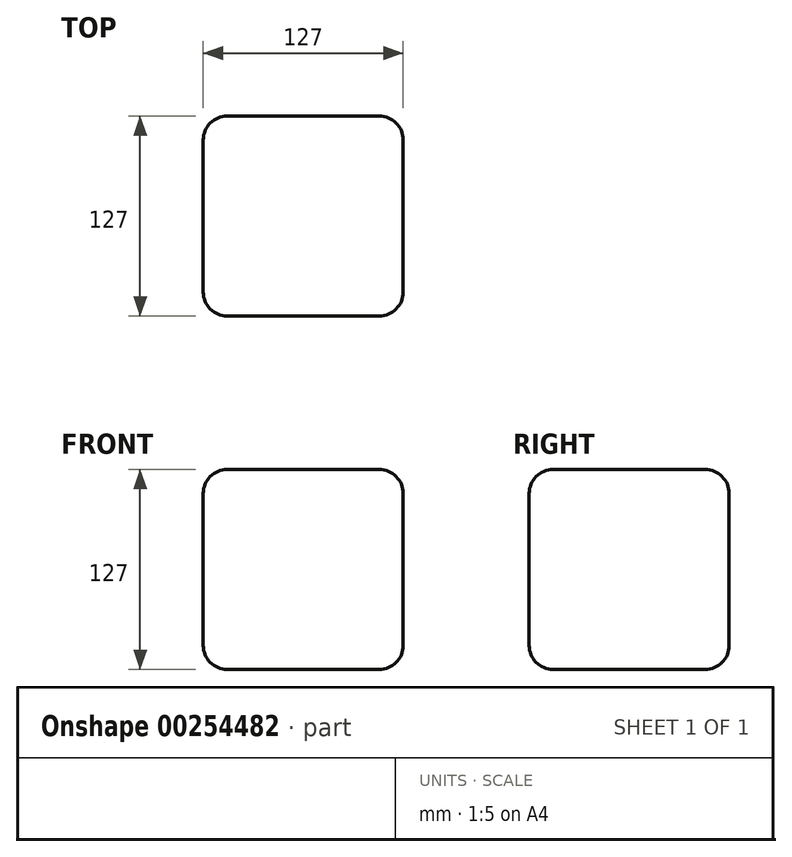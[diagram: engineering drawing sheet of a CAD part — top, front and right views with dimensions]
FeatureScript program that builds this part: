
annotation { "Feature Type Name" : "Feature", "Feature Type Description" : "" }
export const myFeature = defineFeature(function(context is Context, id is Id, definition is map)
    precondition{}
    {
        {
            var Q0;
            Q0=qCreatedBy(makeId("Front.planeOp"),FACE);
            var sketch = newSketch(context, id + "F0", { "sketchPlane" : qUnion([Q0])});
            skLineSegment(sketch, "E0.bottom", {"start": v(-64.7, 75.53) * mm, "end": v(62.3, 75.53) * mm});
            skLineSegment(sketch, "E0.top", {"start": v(-64.7, -51.47) * mm, "end": v(62.3, -51.47) * mm});
            skLineSegment(sketch, "E0.left", {"start": v(-64.7, 75.53) * mm, "end": v(-64.7, -51.47) * mm});
            skLineSegment(sketch, "E0.right", {"start": v(62.3, 75.53) * mm, "end": v(62.3, -51.47) * mm});
            skSolve(sketch);
        }
        {
            var Q0;
            Q0=makeQuery(id+"F0.imprint","IMPRINT",FACE,{"disambiguationData":[TD([[makeQuery(id+"F0.imprint","IMPRINT",EDGE,{"derivedFrom":sQuery(id+"F0.wireOp",EDGE,"E0.bottom")}),-1.0]])]});
            extrude(context, id + "F1", {"entities" : qUnion([Q0]), "depth" : 127 * mm});
        }
        {
            var Q0;
            Q0=makeQuery(id+"F1.opExtrude","SWEPT_FACE",FACE,{"disambiguationData":[OSD([sQuery(id+"F0.wireOp",EDGE,"E0.bottom")])]});
            var Q1;
            Q1=makeQuery(id+"F1.opExtrude","CAP_FACE",FACE,{"disambiguationData":[OSD([sQuery(id+"F0.wireOp",EDGE,"E0.bottom"),sQuery(id+"F0.wireOp",EDGE,"E0.top"),sQuery(id+"F0.wireOp",EDGE,"E0.left"),sQuery(id+"F0.wireOp",EDGE,"E0.right")])],"isStart":false});
            var Q2;
            Q2=makeQuery(id+"F1.opExtrude","SWEPT_FACE",FACE,{"disambiguationData":[OSD([sQuery(id+"F0.wireOp",EDGE,"E0.right")])]});
            var Q3;
            Q3=makeQuery(id+"F1.opExtrude","SWEPT_FACE",FACE,{"disambiguationData":[OSD([sQuery(id+"F0.wireOp",EDGE,"E0.left")])]});
            var Q4;
            Q4=makeQuery(id+"F1.opExtrude","CAP_FACE",FACE,{"disambiguationData":[OSD([sQuery(id+"F0.wireOp",EDGE,"E0.bottom"),sQuery(id+"F0.wireOp",EDGE,"E0.top"),sQuery(id+"F0.wireOp",EDGE,"E0.left"),sQuery(id+"F0.wireOp",EDGE,"E0.right")])],"isStart":true});
            fillet(context, id + "F2", {"entities" : qUnion([Q0, Q1, Q2, Q3, Q4]), "radius" : 15.24 * mm, "tangentPropagation" : true, "allowEdgeOverflow" : false});
        }
    });
